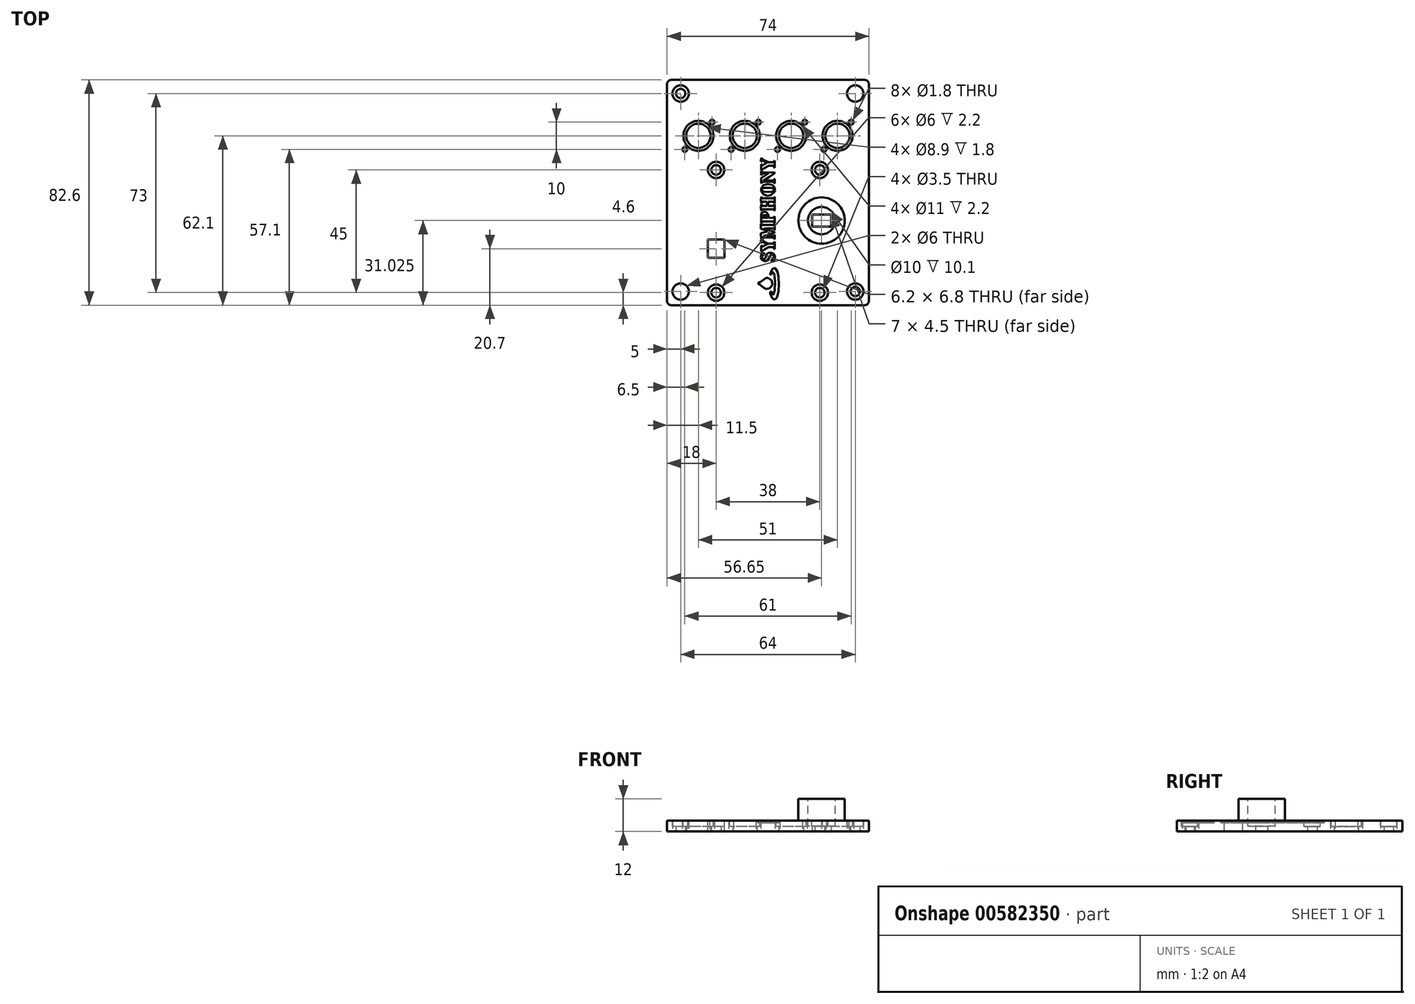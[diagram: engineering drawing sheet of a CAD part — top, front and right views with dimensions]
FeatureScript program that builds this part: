
annotation { "Feature Type Name" : "Feature", "Feature Type Description" : "" }
export const myFeature = defineFeature(function(context is Context, id is Id, definition is map)
    precondition{}
    {
        {
            var Q0;
            Q0=qCreatedBy(makeId("Top.planeOp"),FACE);
            var sketch = newSketch(context, id + "F0", { "sketchPlane" : qUnion([Q0])});
            skLineSegment(sketch, "E0.bottom", {"start": v(22.5, -9) * mm, "end": v(22.5, -61) * mm, "construction": true});
            skLineSegment(sketch, "E0.top", {"start": v(-22.5, -9) * mm, "end": v(-22.5, -61) * mm, "construction": true});
            skLineSegment(sketch, "E0.left", {"start": v(22.5, -9) * mm, "end": v(-22.5, -9) * mm, "construction": true});
            skLineSegment(sketch, "E0.right", {"start": v(22.5, -61) * mm, "end": v(-22.5, -61) * mm, "construction": true});
            skPoint(sketch, "E0.middle", {"position": v(0, -35) * mm});
            skCircle(sketch, "E1", {"center": v(-19, -57.5) * mm, "radius": 1.5 * mm, "construction": true});
            skCircle(sketch, "E2.cCircle", {"center": v(-19, -57.5) * mm, "radius": 2.75 * mm, "construction": true});
            skLineSegment(sketch, "E2.0", {"start": v(-20.59, -54.75) * mm, "end": v(-17.41, -54.75) * mm, "construction": true});
            skLineSegment(sketch, "E2.1", {"start": v(-17.41, -54.75) * mm, "end": v(-15.82, -57.5) * mm, "construction": true});
            skLineSegment(sketch, "E2.2", {"start": v(-15.82, -57.5) * mm, "end": v(-17.41, -60.25) * mm, "construction": true});
            skLineSegment(sketch, "E2.3", {"start": v(-17.41, -60.25) * mm, "end": v(-20.59, -60.25) * mm, "construction": true});
            skLineSegment(sketch, "E2.4", {"start": v(-20.59, -60.25) * mm, "end": v(-22.18, -57.5) * mm, "construction": true});
            skLineSegment(sketch, "E2.5", {"start": v(-22.18, -57.5) * mm, "end": v(-20.59, -54.75) * mm, "construction": true});
            skPoint(sketch, "E2.0.midPoint", {"position": v(-19, -54.75) * mm});
            skLineSegment(sketch, "E3.MirrorCS", {"start": v(-20.59, -15.25) * mm, "end": v(-17.41, -15.25) * mm, "construction": true});
            skCircle(sketch, "E4.MirrorC", {"center": v(-19, -12.5) * mm, "radius": 1.5 * mm, "construction": true});
            skCircle(sketch, "E5.MirrorC", {"center": v(-19, -12.5) * mm, "radius": 2.75 * mm, "construction": true});
            skLineSegment(sketch, "E6.MirrorCS", {"start": v(-17.41, -15.25) * mm, "end": v(-15.82, -12.5) * mm, "construction": true});
            skPoint(sketch, "E7.MirrorP", {"position": v(-19, -15.25) * mm});
            skLineSegment(sketch, "E8.MirrorCS", {"start": v(-22.18, -12.5) * mm, "end": v(-20.59, -15.25) * mm, "construction": true});
            skLineSegment(sketch, "E9.MirrorCS", {"start": v(-20.59, -9.75) * mm, "end": v(-22.18, -12.5) * mm, "construction": true});
            skLineSegment(sketch, "E10.MirrorCS", {"start": v(-15.82, -12.5) * mm, "end": v(-17.41, -9.75) * mm, "construction": true});
            skLineSegment(sketch, "E11.MirrorCS", {"start": v(-17.41, -9.75) * mm, "end": v(-20.59, -9.75) * mm, "construction": true});
            skLineSegment(sketch, "E12.MirrorCS", {"start": v(20.59, -15.25) * mm, "end": v(17.41, -15.25) * mm, "construction": true});
            skLineSegment(sketch, "E13.MirrorCS", {"start": v(22.18, -57.5) * mm, "end": v(20.59, -54.75) * mm, "construction": true});
            skLineSegment(sketch, "E14.MirrorCS", {"start": v(20.59, -60.25) * mm, "end": v(22.18, -57.5) * mm, "construction": true});
            skLineSegment(sketch, "E15.MirrorCS", {"start": v(15.82, -57.5) * mm, "end": v(17.41, -60.25) * mm, "construction": true});
            skLineSegment(sketch, "E16.MirrorCS", {"start": v(17.41, -54.75) * mm, "end": v(15.82, -57.5) * mm, "construction": true});
            skLineSegment(sketch, "E17.MirrorCS", {"start": v(20.59, -54.75) * mm, "end": v(17.41, -54.75) * mm, "construction": true});
            skLineSegment(sketch, "E18.MirrorCS", {"start": v(20.59, -9.75) * mm, "end": v(22.18, -12.5) * mm, "construction": true});
            skLineSegment(sketch, "E19.MirrorCS", {"start": v(17.41, -9.75) * mm, "end": v(20.59, -9.75) * mm, "construction": true});
            skLineSegment(sketch, "E20.MirrorCS", {"start": v(22.18, -12.5) * mm, "end": v(20.59, -15.25) * mm, "construction": true});
            skLineSegment(sketch, "E21.MirrorCS", {"start": v(15.82, -12.5) * mm, "end": v(17.41, -9.75) * mm, "construction": true});
            skLineSegment(sketch, "E22.MirrorCS", {"start": v(17.41, -15.25) * mm, "end": v(15.82, -12.5) * mm, "construction": true});
            skLineSegment(sketch, "E23.MirrorCS", {"start": v(17.41, -60.25) * mm, "end": v(20.59, -60.25) * mm, "construction": true});
            skCircle(sketch, "E24.MirrorC", {"center": v(19, -57.5) * mm, "radius": 2.75 * mm, "construction": true});
            skPoint(sketch, "E25.MirrorP", {"position": v(19, -15.25) * mm});
            skCircle(sketch, "E26.MirrorC", {"center": v(19, -57.5) * mm, "radius": 1.5 * mm, "construction": true});
            skCircle(sketch, "E27.MirrorC", {"center": v(19, -12.5) * mm, "radius": 2.75 * mm, "construction": true});
            skCircle(sketch, "E28.MirrorC", {"center": v(19, -12.5) * mm, "radius": 1.5 * mm, "construction": true});
            skPoint(sketch, "E29.MirrorP", {"position": v(19, -54.75) * mm});
            skLineSegment(sketch, "E30.bottom", {"start": v(16.9, -32.65) * mm, "end": v(16.9, -29.5) * mm, "construction": true});
            skLineSegment(sketch, "E30.top", {"start": v(22.4, -32.65) * mm, "end": v(22.4, -29.5) * mm, "construction": true});
            skLineSegment(sketch, "E30.left", {"start": v(16.9, -32.65) * mm, "end": v(22.4, -32.65) * mm, "construction": true});
            skLineSegment(sketch, "E30.right", {"start": v(16.9, -29.5) * mm, "end": v(22.4, -29.5) * mm, "construction": true});
            skLineSegment(sketch, "E31", {"start": v(16.9, -32.65) * mm, "end": v(22.4, -29.5) * mm, "construction": true});
            skLineSegment(sketch, "E32", {"start": v(16.9, -29.5) * mm, "end": v(22.4, -32.65) * mm, "construction": true});
            skSolve(sketch);
        }
        {
            var Q0;
            Q0=qCreatedBy(makeId("Top.planeOp"),FACE);
            var sketch = newSketch(context, id + "F1", { "sketchPlane" : qUnion([Q0])});
            skLineSegment(sketch, "E33.bottom", {"start": v(-18, -7.5) * mm, "end": v(-33, -7.5) * mm, "construction": true});
            skLineSegment(sketch, "E33.top", {"start": v(-18, 7.5) * mm, "end": v(-33, 7.5) * mm, "construction": true});
            skLineSegment(sketch, "E33.left", {"start": v(-18, -7.5) * mm, "end": v(-18, 7.5) * mm, "construction": true});
            skLineSegment(sketch, "E33.right", {"start": v(-33, -7.5) * mm, "end": v(-33, 7.5) * mm, "construction": true});
            skCircle(sketch, "E34", {"center": v(-30.5, 5) * mm, "radius": 0.9 * mm});
            skCircle(sketch, "E35.MirrorC", {"center": v(-20.5, 5) * mm, "radius": 0.9 * mm});
            skCircle(sketch, "E36.MirrorC", {"center": v(-30.5, -5) * mm, "radius": 0.9 * mm});
            skCircle(sketch, "E37.MirrorC", {"center": v(-20.5, -5) * mm, "radius": 0.9 * mm});
            skCircle(sketch, "E38.1.0.0", {"center": v(-13.5, -5) * mm, "radius": 0.9 * mm});
            skCircle(sketch, "E38.1.0.1", {"center": v(-13.5, 5) * mm, "radius": 0.9 * mm});
            skLineSegment(sketch, "E38.1.0.2", {"start": v(-16, -7.5) * mm, "end": v(-16, 7.5) * mm, "construction": true});
            skLineSegment(sketch, "E38.1.0.3", {"start": v(-1, -7.5) * mm, "end": v(-1, 7.5) * mm, "construction": true});
            skCircle(sketch, "E38.1.0.4", {"center": v(-3.5, 5) * mm, "radius": 0.9 * mm});
            skCircle(sketch, "E38.1.0.5", {"center": v(-3.5, -5) * mm, "radius": 0.9 * mm});
            skLineSegment(sketch, "E38.1.0.6", {"start": v(-1, -7.5) * mm, "end": v(-16, -7.5) * mm, "construction": true});
            skLineSegment(sketch, "E38.1.0.7", {"start": v(-1, 7.5) * mm, "end": v(-16, 7.5) * mm, "construction": true});
            skCircle(sketch, "E38.2.0.0", {"center": v(3.5, -5) * mm, "radius": 0.9 * mm});
            skCircle(sketch, "E38.2.0.1", {"center": v(3.5, 5) * mm, "radius": 0.9 * mm});
            skLineSegment(sketch, "E38.2.0.2", {"start": v(1, -7.5) * mm, "end": v(1, 7.5) * mm, "construction": true});
            skLineSegment(sketch, "E38.2.0.3", {"start": v(16, -7.5) * mm, "end": v(16, 7.5) * mm, "construction": true});
            skCircle(sketch, "E38.2.0.4", {"center": v(13.5, 5) * mm, "radius": 0.9 * mm});
            skCircle(sketch, "E38.2.0.5", {"center": v(13.5, -5) * mm, "radius": 0.9 * mm});
            skLineSegment(sketch, "E38.2.0.6", {"start": v(16, -7.5) * mm, "end": v(1, -7.5) * mm, "construction": true});
            skLineSegment(sketch, "E38.2.0.7", {"start": v(16, 7.5) * mm, "end": v(1, 7.5) * mm, "construction": true});
            skCircle(sketch, "E38.3.0.0", {"center": v(20.5, -5) * mm, "radius": 0.9 * mm});
            skCircle(sketch, "E38.3.0.1", {"center": v(20.5, 5) * mm, "radius": 0.9 * mm});
            skLineSegment(sketch, "E38.3.0.2", {"start": v(18, -7.5) * mm, "end": v(18, 7.5) * mm, "construction": true});
            skLineSegment(sketch, "E38.3.0.3", {"start": v(33, -7.5) * mm, "end": v(33, 7.5) * mm, "construction": true});
            skCircle(sketch, "E38.3.0.4", {"center": v(30.5, 5) * mm, "radius": 0.9 * mm});
            skCircle(sketch, "E38.3.0.5", {"center": v(30.5, -5) * mm, "radius": 0.9 * mm});
            skLineSegment(sketch, "E38.3.0.6", {"start": v(33, -7.5) * mm, "end": v(18, -7.5) * mm, "construction": true});
            skLineSegment(sketch, "E38.3.0.7", {"start": v(33, 7.5) * mm, "end": v(18, 7.5) * mm, "construction": true});
            skLineSegment(sketch, "E38.direction1", {"start": v(-33, -7.5) * mm, "end": v(-16, -7.5) * mm, "construction": true});
            skLineSegment(sketch, "E39.top", {"start": v(-37, -62.1) * mm, "end": v(37, -62.1) * mm});
            skLineSegment(sketch, "E39.left", {"start": v(-37, 10.5) * mm, "end": v(-37, -62.1) * mm});
            skLineSegment(sketch, "E39.right", {"start": v(37, 10.5) * mm, "end": v(37, -62.1) * mm});
            skPoint(sketch, "E40.0", {"position": v(-19, -12.5) * mm});
            skCircle(sketch, "E41", {"center": v(-19, -12.5) * mm, "radius": 1.75 * mm});
            skCircle(sketch, "E42.MirrorC", {"center": v(19, -12.5) * mm, "radius": 1.75 * mm});
            skCircle(sketch, "E43.MirrorC", {"center": v(19, -57.5) * mm, "radius": 1.75 * mm});
            skCircle(sketch, "E44.MirrorC", {"center": v(-19, -57.5) * mm, "radius": 1.75 * mm});
            skLineSegment(sketch, "E45.direction1", {"start": v(-25.5, 0) * mm, "end": v(-8.5, 0) * mm, "construction": true});
            skLineSegment(sketch, "E46.top", {"start": v(-37, 20.5) * mm, "end": v(37, 20.5) * mm});
            skLineSegment(sketch, "E46.left", {"start": v(-37, 10.5) * mm, "end": v(-37, 20.5) * mm});
            skLineSegment(sketch, "E46.right", {"start": v(37, 10.5) * mm, "end": v(37, 20.5) * mm});
            skCircle(sketch, "E47", {"center": v(-32, 15.5) * mm, "radius": 1.7 * mm});
            skCircle(sketch, "E48", {"center": v(-32, 15.5) * mm, "radius": 3 * mm});
            skCircle(sketch, "E49.MirrorC", {"center": v(32, 15.5) * mm, "radius": 3 * mm});
            skCircle(sketch, "E50.MirrorC", {"center": v(32, 15.5) * mm, "radius": 1.7 * mm});
            skLineSegment(sketch, "E51", {"start": v(-37, -20.8) * mm, "end": v(37, -20.8) * mm, "construction": true});
            skCircle(sketch, "E52.MirrorC", {"center": v(32, -57.1) * mm, "radius": 1.7 * mm});
            skCircle(sketch, "E53.MirrorC", {"center": v(32, -57.1) * mm, "radius": 3 * mm});
            skCircle(sketch, "E54.MirrorC", {"center": v(-32, -57.1) * mm, "radius": 3 * mm});
            skCircle(sketch, "E55.MirrorC", {"center": v(-32, -57.1) * mm, "radius": 1.7 * mm});
            skCircle(sketch, "E56", {"center": v(-25.5, 0) * mm, "radius": 4.45 * mm});
            skCircle(sketch, "E57.1.0.0", {"center": v(-8.5, 0) * mm, "radius": 4.45 * mm});
            skCircle(sketch, "E57.2.0.0", {"center": v(8.5, 0) * mm, "radius": 4.45 * mm});
            skCircle(sketch, "E57.3.0.0", {"center": v(25.5, 0) * mm, "radius": 4.45 * mm});
            skPoint(sketch, "E58.0", {"position": v(19.65, -31.08) * mm});
            skLineSegment(sketch, "E59.bottom", {"start": v(23.15, -33.33) * mm, "end": v(16.15, -33.33) * mm});
            skLineSegment(sketch, "E59.top", {"start": v(23.15, -28.83) * mm, "end": v(16.15, -28.83) * mm});
            skLineSegment(sketch, "E59.left", {"start": v(23.15, -33.33) * mm, "end": v(23.15, -28.83) * mm});
            skLineSegment(sketch, "E59.right", {"start": v(16.15, -33.33) * mm, "end": v(16.15, -28.83) * mm});
            skCircle(sketch, "E60", {"center": v(19.65, -31.08) * mm, "radius": 5 * mm});
            skCircle(sketch, "E61", {"center": v(19.65, -31.08) * mm, "radius": 8.5 * mm});
            skSolve(sketch);
        }
        {
            var Q0;
            Q0=makeQuery(id+"F1.imprint","IMPRINT",FACE,{"disambiguationData":[TD([[makeQuery(id+"F1.imprint","IMPRINT",EDGE,{"derivedFrom":sQuery(id+"F1.wireOp",EDGE,"E34")}),-1.0]])]});
            var Q1;
            Q1=makeQuery(id+"F1.imprint","IMPRINT",FACE,{"disambiguationData":[TD([[makeQuery(id+"F1.imprint","IMPRINT",EDGE,{"derivedFrom":sQuery(id+"F1.wireOp",EDGE,"E47")}),-1.0]])]});
            var Q2;
            Q2=makeQuery(id+"F1.imprint","IMPRINT",FACE,{"disambiguationData":[TD([[makeQuery(id+"F1.imprint","IMPRINT",EDGE,{"derivedFrom":sQuery(id+"F1.wireOp",EDGE,"E49.MirrorC")}),-1.0]])]});
            var Q3;
            Q3=makeQuery(id+"F1.imprint","IMPRINT",FACE,{"disambiguationData":[TD([[makeQuery(id+"F1.imprint","IMPRINT",EDGE,{"derivedFrom":sQuery(id+"F1.wireOp",EDGE,"E54.MirrorC")}),-1.0]])]});
            var Q4;
            Q4=makeQuery(id+"F1.imprint","IMPRINT",FACE,{"disambiguationData":[TD([[makeQuery(id+"F1.imprint","IMPRINT",EDGE,{"derivedFrom":sQuery(id+"F1.wireOp",EDGE,"E52.MirrorC")}),-1.0]])]});
            var Q5;
            Q5=makeQuery(id+"F1.imprint","IMPRINT",FACE,{"disambiguationData":[TD([[makeQuery(id+"F1.imprint","IMPRINT",EDGE,{"derivedFrom":sQuery(id+"F1.wireOp",EDGE,"E34")}),1.0]])]});
            var Q6;
            Q6=makeQuery(id+"F1.imprint","IMPRINT",FACE,{"disambiguationData":[TD([[makeQuery(id+"F1.imprint","IMPRINT",EDGE,{"derivedFrom":sQuery(id+"F1.wireOp",EDGE,"E38.2.0.0")}),-1.0]])]});
            var Q7;
            Q7=makeQuery(id+"F1.imprint","IMPRINT",FACE,{"disambiguationData":[TD([[makeQuery(id+"F1.imprint","IMPRINT",EDGE,{"derivedFrom":sQuery(id+"F1.wireOp",EDGE,"E36.MirrorC")}),-1.0]])]});
            var Q8;
            Q8=makeQuery(id+"F1.imprint","IMPRINT",FACE,{"disambiguationData":[TD([[makeQuery(id+"F1.imprint","IMPRINT",EDGE,{"derivedFrom":sQuery(id+"F1.wireOp",EDGE,"E37.MirrorC")}),1.0]])]});
            var Q9;
            Q9=makeQuery(id+"F1.imprint","IMPRINT",FACE,{"disambiguationData":[TD([[makeQuery(id+"F1.imprint","IMPRINT",EDGE,{"derivedFrom":sQuery(id+"F1.wireOp",EDGE,"E38.1.0.0")}),-1.0]])]});
            var Q10;
            Q10=makeQuery(id+"F1.imprint","IMPRINT",FACE,{"disambiguationData":[TD([[makeQuery(id+"F1.imprint","IMPRINT",EDGE,{"derivedFrom":sQuery(id+"F1.wireOp",EDGE,"E38.1.0.5")}),1.0]])]});
            var Q11;
            Q11=makeQuery(id+"F1.imprint","IMPRINT",FACE,{"disambiguationData":[TD([[makeQuery(id+"F1.imprint","IMPRINT",EDGE,{"derivedFrom":sQuery(id+"F1.wireOp",EDGE,"E38.2.0.12")}),1.0]])]});
            var Q12;
            Q12=makeQuery(id+"F1.imprint","IMPRINT",FACE,{"disambiguationData":[TD([[makeQuery(id+"F1.imprint","IMPRINT",EDGE,{"derivedFrom":sQuery(id+"F1.wireOp",EDGE,"E38.1.0.12")}),1.0]])]});
            var Q13;
            Q13=makeQuery(id+"F1.imprint","IMPRINT",FACE,{"disambiguationData":[TD([[makeQuery(id+"F1.imprint","IMPRINT",EDGE,{"derivedFrom":sQuery(id+"F1.wireOp",EDGE,"0d3dec74-ecaa-4266-b990-dcd2288d9d95")}),1.0]])]});
            var Q14;
            Q14=makeQuery(id+"F1.imprint","IMPRINT",FACE,{"disambiguationData":[TD([[makeQuery(id+"F1.imprint","IMPRINT",EDGE,{"derivedFrom":sQuery(id+"F1.wireOp",EDGE,"f5867afd-0dbe-4015-8089-30a12c86c954")}),1.0]])]});
            var Q15;
            Q15=makeQuery(id+"F1.imprint","IMPRINT",FACE,{"disambiguationData":[TD([[makeQuery(id+"F1.imprint","IMPRINT",EDGE,{"derivedFrom":sQuery(id+"F1.wireOp",EDGE,"70b2c587-75d0-4c69-bc02-c068b628aa1f")}),1.0]])]});
            var Q16;
            Q16=makeQuery(id+"F1.imprint","IMPRINT",FACE,{"disambiguationData":[TD([[makeQuery(id+"F1.imprint","IMPRINT",EDGE,{"derivedFrom":sQuery(id+"F1.wireOp",EDGE,"E38.1.0.10")}),1.0]])]});
            var Q17;
            Q17=makeQuery(id+"F1.imprint","IMPRINT",FACE,{"disambiguationData":[TD([[makeQuery(id+"F1.imprint","IMPRINT",EDGE,{"derivedFrom":sQuery(id+"F1.wireOp",EDGE,"E38.1.0.11")}),1.0]])]});
            var Q18;
            Q18=makeQuery(id+"F1.imprint","IMPRINT",FACE,{"disambiguationData":[TD([[makeQuery(id+"F1.imprint","IMPRINT",EDGE,{"derivedFrom":sQuery(id+"F1.wireOp",EDGE,"E38.2.0.10")}),1.0]])]});
            var Q19;
            Q19=makeQuery(id+"F1.imprint","IMPRINT",FACE,{"disambiguationData":[TD([[makeQuery(id+"F1.imprint","IMPRINT",EDGE,{"derivedFrom":sQuery(id+"F1.wireOp",EDGE,"E38.2.0.11")}),1.0]])]});
            var Q20;
            Q20=makeQuery(id+"F1.imprint","IMPRINT",FACE,{"disambiguationData":[TD([[makeQuery(id+"F1.imprint","IMPRINT",EDGE,{"derivedFrom":sQuery(id+"F1.wireOp",EDGE,"E38.3.0.0")}),-1.0]])]});
            var Q21;
            Q21=makeQuery(id+"F1.imprint","IMPRINT",FACE,{"disambiguationData":[TD([[makeQuery(id+"F1.imprint","IMPRINT",EDGE,{"derivedFrom":sQuery(id+"F1.wireOp",EDGE,"E38.3.0.1")}),1.0]])]});
            var Q22;
            Q22=makeQuery(id+"F1.imprint","IMPRINT",FACE,{"disambiguationData":[TD([[makeQuery(id+"F1.imprint","IMPRINT",EDGE,{"derivedFrom":sQuery(id+"F1.wireOp",EDGE,"0d3dec74-ecaa-4266-b990-dcd2288d9d95")}),-1.0]])]});
            var Q23;
            Q23=makeQuery(id+"F1.imprint","IMPRINT",FACE,{"disambiguationData":[TD([[makeQuery(id+"F1.imprint","IMPRINT",EDGE,{"derivedFrom":sQuery(id+"F1.wireOp",EDGE,"E38.1.0.10")}),-1.0]])]});
            var Q24;
            Q24=makeQuery(id+"F1.imprint","IMPRINT",FACE,{"disambiguationData":[TD([[makeQuery(id+"F1.imprint","IMPRINT",EDGE,{"derivedFrom":sQuery(id+"F1.wireOp",EDGE,"E38.2.0.10")}),-1.0]])]});
            var Q25;
            Q25=makeQuery(id+"F1.imprint","IMPRINT",FACE,{"disambiguationData":[TD([[makeQuery(id+"F1.imprint","IMPRINT",EDGE,{"derivedFrom":sQuery(id+"F1.wireOp",EDGE,"E38.2.0.4")}),-1.0]])]});
            var Q26;
            Q26=makeQuery(id+"F1.imprint","IMPRINT",FACE,{"disambiguationData":[TD([[makeQuery(id+"F1.imprint","IMPRINT",EDGE,{"derivedFrom":sQuery(id+"F1.wireOp",EDGE,"E38.2.0.1")}),1.0]])]});
            var Q27;
            Q27=makeQuery(id+"F1.imprint","IMPRINT",FACE,{"disambiguationData":[TD([[makeQuery(id+"F1.imprint","IMPRINT",EDGE,{"derivedFrom":sQuery(id+"F1.wireOp",EDGE,"E35.MirrorC")}),-1.0]])]});
            var Q28;
            Q28=makeQuery(id+"F1.imprint","IMPRINT",FACE,{"disambiguationData":[TD([[makeQuery(id+"F1.imprint","IMPRINT",EDGE,{"derivedFrom":sQuery(id+"F1.wireOp",EDGE,"E38.2.0.5")}),1.0]])]});
            var Q29;
            Q29=makeQuery(id+"F1.imprint","IMPRINT",FACE,{"disambiguationData":[TD([[makeQuery(id+"F1.imprint","IMPRINT",EDGE,{"derivedFrom":sQuery(id+"F1.wireOp",EDGE,"E38.1.0.1")}),1.0]])]});
            var Q30;
            Q30=makeQuery(id+"F1.imprint","IMPRINT",FACE,{"disambiguationData":[TD([[makeQuery(id+"F1.imprint","IMPRINT",EDGE,{"derivedFrom":sQuery(id+"F1.wireOp",EDGE,"E38.1.0.4")}),-1.0]])]});
            var Q31;
            Q31=makeQuery(id+"F1.imprint","IMPRINT",FACE,{"disambiguationData":[TD([[makeQuery(id+"F1.imprint","IMPRINT",EDGE,{"derivedFrom":sQuery(id+"F1.wireOp",EDGE,"E38.3.0.4")}),-1.0]])]});
            var Q32;
            Q32=makeQuery(id+"F1.imprint","IMPRINT",FACE,{"disambiguationData":[TD([[makeQuery(id+"F1.imprint","IMPRINT",EDGE,{"derivedFrom":sQuery(id+"F1.wireOp",EDGE,"E38.3.0.5")}),1.0]])]});
            var Q33;
            Q33=makeQuery(id+"F1.imprint","IMPRINT",FACE,{"disambiguationData":[TD([[makeQuery(id+"F1.imprint","IMPRINT",EDGE,{"derivedFrom":sQuery(id+"F1.wireOp",EDGE,"E38.3.0.10")}),-1.0]])]});
            var Q34;
            Q34=makeQuery(id+"F1.imprint","IMPRINT",FACE,{"disambiguationData":[TD([[makeQuery(id+"F1.imprint","IMPRINT",EDGE,{"derivedFrom":sQuery(id+"F1.wireOp",EDGE,"E38.3.0.10")}),1.0]])]});
            var Q35;
            Q35=makeQuery(id+"F1.imprint","IMPRINT",FACE,{"disambiguationData":[TD([[makeQuery(id+"F1.imprint","IMPRINT",EDGE,{"derivedFrom":sQuery(id+"F1.wireOp",EDGE,"E38.3.0.11")}),1.0]])]});
            var Q36;
            Q36=makeQuery(id+"F1.imprint","IMPRINT",FACE,{"disambiguationData":[TD([[makeQuery(id+"F1.imprint","IMPRINT",EDGE,{"derivedFrom":sQuery(id+"F1.wireOp",EDGE,"E38.3.0.12")}),1.0]])]});
            var Q37;
            Q37=makeQuery(id+"F1.imprint","IMPRINT",FACE,{"disambiguationData":[TD([[makeQuery(id+"F1.imprint","IMPRINT",EDGE,{"derivedFrom":sQuery(id+"F1.wireOp",EDGE,"E60")}),-1.0]])]});
            var Q38;
            Q38=makeQuery(id+"F1.imprint","IMPRINT",FACE,{"disambiguationData":[TD([[makeQuery(id+"F1.imprint","IMPRINT",EDGE,{"derivedFrom":sQuery(id+"F1.wireOp",EDGE,"E59.bottom")}),1.0]])]});
            extrude(context, id + "F2", {"entities" : qUnion([Q0, Q1, Q2, Q3, Q4, Q5, Q6, Q7, Q8, Q9, Q10, Q11, Q12, Q13, Q14, Q15, Q16, Q17, Q18, Q19, Q20, Q21, Q22, Q23, Q24, Q25, Q26, Q27, Q28, Q29, Q30, Q31, Q32, Q33, Q34, Q35, Q36, Q37, Q38]), "depth" : 4 * mm, "offsetDistance" : 25 * mm});
        }
        {
            var Q0;
            Q0=makeQuery(id+"F2.opExtrude","SWEPT_EDGE",EDGE,{"disambiguationData":[OSD([sQuery(id+"F1.wireOp",EDGE,"E39.top"),sQuery(id+"F1.wireOp",EDGE,"E39.left")])]});
            var Q1;
            Q1=makeQuery(id+"F2.opExtrude","SWEPT_EDGE",EDGE,{"disambiguationData":[OSD([sQuery(id+"F1.wireOp",EDGE,"E39.top"),sQuery(id+"F1.wireOp",EDGE,"E39.right")])]});
            var Q2;
            Q2=makeQuery(id+"F2.opExtrude","SWEPT_EDGE",EDGE,{"disambiguationData":[OSD([sQuery(id+"F1.wireOp",EDGE,"E46.top"),sQuery(id+"F1.wireOp",EDGE,"E46.right")])]});
            var Q3;
            Q3=makeQuery(id+"F2.opExtrude","SWEPT_EDGE",EDGE,{"disambiguationData":[OSD([sQuery(id+"F1.wireOp",EDGE,"E46.top"),sQuery(id+"F1.wireOp",EDGE,"E46.left")])]});
            fillet(context, id + "F3", {"entities" : qUnion([Q0, Q1, Q2, Q3]), "radius" : 1.5 * mm, "tangentPropagation" : true, "allowEdgeOverflow" : false});
        }
        {
            var Q0;
            Q0=makeQuery(id+"F2.opExtrude","CAP_FACE",FACE,{"disambiguationData":[OSD([sQuery(id+"F1.wireOp",EDGE,"E39.top"),sQuery(id+"F1.wireOp",EDGE,"E39.left"),sQuery(id+"F1.wireOp",EDGE,"E39.right"),sQuery(id+"F1.wireOp",EDGE,"ZtF59OV2-kfJq-xDQm-ky9b-vxAiDFjwtKrt.bottom"),sQuery(id+"F1.wireOp",EDGE,"ZtF59OV2-kfJq-xDQm-ky9b-vxAiDFjwtKrt.top"),sQuery(id+"F1.wireOp",EDGE,"ZtF59OV2-kfJq-xDQm-ky9b-vxAiDFjwtKrt.left"),sQuery(id+"F1.wireOp",EDGE,"ZtF59OV2-kfJq-xDQm-ky9b-vxAiDFjwtKrt.right"),sQuery(id+"F1.wireOp",EDGE,"OfxVgRd8-8Rll-FesW-K7WL-WmYAdUh40JBy.bottom"),sQuery(id+"F1.wireOp",EDGE,"OfxVgRd8-8Rll-FesW-K7WL-WmYAdUh40JBy.top"),sQuery(id+"F1.wireOp",EDGE,"OfxVgRd8-8Rll-FesW-K7WL-WmYAdUh40JBy.left"),sQuery(id+"F1.wireOp",EDGE,"OfxVgRd8-8Rll-FesW-K7WL-WmYAdUh40JBy.right"),sQuery(id+"F1.wireOp",EDGE,"5421b44d-8772-4a96-8ed2-b48facbd643a.trimOffspring"),sQuery(id+"F1.wireOp",EDGE,"446a1e51-2a2d-4a3d-b0c0-7d5b57a94e87.trimOffspring"),sQuery(id+"F1.wireOp",EDGE,"e6be4eb3-bc97-4f03-aafd-c3c38b5d689d.trimOffspring"),sQuery(id+"F1.wireOp",EDGE,"9b8aff40-883d-4fe7-9ef0-59bda9a35524.trimOffspring"),sQuery(id+"F1.wireOp",EDGE,"E41"),sQuery(id+"F1.wireOp",EDGE,"E42.MirrorC"),sQuery(id+"F1.wireOp",EDGE,"E43.MirrorC"),sQuery(id+"F1.wireOp",EDGE,"E44.MirrorC"),sQuery(id+"F1.wireOp",EDGE,"E46.top"),sQuery(id+"F1.wireOp",EDGE,"E46.left"),sQuery(id+"F1.wireOp",EDGE,"E46.right"),sQuery(id+"F1.wireOp",EDGE,"E47"),sQuery(id+"F1.wireOp",EDGE,"E50.MirrorC"),sQuery(id+"F1.wireOp",EDGE,"E52.MirrorC"),sQuery(id+"F1.wireOp",EDGE,"E55.MirrorC"),sQuery(id+"F1.wireOp",EDGE,"E56"),sQuery(id+"F1.wireOp",EDGE,"E57.1.0.0"),sQuery(id+"F1.wireOp",EDGE,"E57.2.0.0"),sQuery(id+"F1.wireOp",EDGE,"E57.3.0.0")])],"isStart":false});
            var sketch = newSketch(context, id + "F4", { "sketchPlane" : qUnion([Q0])});
            skCircle(sketch, "E62.0", {"center": v(-32, -57.1) * mm, "radius": 3 * mm});
            skCircle(sketch, "E63.0", {"center": v(-32, 15.5) * mm, "radius": 3 * mm});
            skCircle(sketch, "E64.0", {"center": v(32, 15.5) * mm, "radius": 3 * mm});
            skCircle(sketch, "E65.0", {"center": v(32, -57.1) * mm, "radius": 3 * mm});
            skCircle(sketch, "E66.0", {"center": v(-19, -57.5) * mm, "radius": 3 * mm});
            skCircle(sketch, "E67.0", {"center": v(19, -57.5) * mm, "radius": 3 * mm});
            skCircle(sketch, "E68.0", {"center": v(19, -12.5) * mm, "radius": 3 * mm});
            skCircle(sketch, "E69.0", {"center": v(-19, -12.5) * mm, "radius": 3 * mm});
            skSolve(sketch);
        }
        {
            var Q0;
            Q0 = qSketchRegion(id + "F4", true);
            extrude(context, id + "F5", {"entities" : qUnion([Q0]), "operationType" : NewBodyOperationType.REMOVE, "oppositeDirection" : true, "depth" : 2.2 * mm, "offsetDistance" : 25 * mm});
        }
        {
            var Q0;
            Q0=makeQuery(id+"F2.opExtrude","CAP_FACE",FACE,{"disambiguationData":[OSD([sQuery(id+"F1.wireOp",EDGE,"E39.top"),sQuery(id+"F1.wireOp",EDGE,"E39.left"),sQuery(id+"F1.wireOp",EDGE,"E39.right"),sQuery(id+"F1.wireOp",EDGE,"ZtF59OV2-kfJq-xDQm-ky9b-vxAiDFjwtKrt.bottom"),sQuery(id+"F1.wireOp",EDGE,"ZtF59OV2-kfJq-xDQm-ky9b-vxAiDFjwtKrt.top"),sQuery(id+"F1.wireOp",EDGE,"ZtF59OV2-kfJq-xDQm-ky9b-vxAiDFjwtKrt.left"),sQuery(id+"F1.wireOp",EDGE,"ZtF59OV2-kfJq-xDQm-ky9b-vxAiDFjwtKrt.right"),sQuery(id+"F1.wireOp",EDGE,"OfxVgRd8-8Rll-FesW-K7WL-WmYAdUh40JBy.bottom"),sQuery(id+"F1.wireOp",EDGE,"OfxVgRd8-8Rll-FesW-K7WL-WmYAdUh40JBy.top"),sQuery(id+"F1.wireOp",EDGE,"OfxVgRd8-8Rll-FesW-K7WL-WmYAdUh40JBy.left"),sQuery(id+"F1.wireOp",EDGE,"OfxVgRd8-8Rll-FesW-K7WL-WmYAdUh40JBy.right"),sQuery(id+"F1.wireOp",EDGE,"5421b44d-8772-4a96-8ed2-b48facbd643a.trimOffspring"),sQuery(id+"F1.wireOp",EDGE,"446a1e51-2a2d-4a3d-b0c0-7d5b57a94e87.trimOffspring"),sQuery(id+"F1.wireOp",EDGE,"e6be4eb3-bc97-4f03-aafd-c3c38b5d689d.trimOffspring"),sQuery(id+"F1.wireOp",EDGE,"9b8aff40-883d-4fe7-9ef0-59bda9a35524.trimOffspring"),sQuery(id+"F1.wireOp",EDGE,"E41"),sQuery(id+"F1.wireOp",EDGE,"E42.MirrorC"),sQuery(id+"F1.wireOp",EDGE,"E43.MirrorC"),sQuery(id+"F1.wireOp",EDGE,"E44.MirrorC"),sQuery(id+"F1.wireOp",EDGE,"E46.top"),sQuery(id+"F1.wireOp",EDGE,"E46.left"),sQuery(id+"F1.wireOp",EDGE,"E46.right"),sQuery(id+"F1.wireOp",EDGE,"E47"),sQuery(id+"F1.wireOp",EDGE,"E50.MirrorC"),sQuery(id+"F1.wireOp",EDGE,"E52.MirrorC"),sQuery(id+"F1.wireOp",EDGE,"E55.MirrorC"),sQuery(id+"F1.wireOp",EDGE,"E56"),sQuery(id+"F1.wireOp",EDGE,"E57.1.0.0"),sQuery(id+"F1.wireOp",EDGE,"E57.2.0.0"),sQuery(id+"F1.wireOp",EDGE,"E57.3.0.0")])],"isStart":false});
            var sketch = newSketch(context, id + "F6", { "sketchPlane" : qUnion([Q0])});
            skPoint(sketch, "E70.0", {"position": v(-25.5, 0) * mm});
            skCircle(sketch, "E71", {"center": v(-25.5, 0) * mm, "radius": 5.5 * mm});
            skCircle(sketch, "E72.1.0.0", {"center": v(-8.5, 0) * mm, "radius": 5.5 * mm});
            skCircle(sketch, "E72.2.0.0", {"center": v(8.5, 0) * mm, "radius": 5.5 * mm});
            skCircle(sketch, "E72.3.0.0", {"center": v(25.5, 0) * mm, "radius": 5.5 * mm});
            skLineSegment(sketch, "E72.direction1", {"start": v(-25.5, 0) * mm, "end": v(-8.5, 0) * mm, "construction": true});
            skSolve(sketch);
        }
        {
            var Q0;
            Q0=makeQuery(id+"F6.imprint","IMPRINT",FACE,{"disambiguationData":[TD([[makeQuery(id+"F6.imprint","IMPRINT",EDGE,{"derivedFrom":sQuery(id+"F6.wireOp",EDGE,"E71")}),1.0]])]});
            var Q1;
            Q1=makeQuery(id+"F6.imprint","IMPRINT",FACE,{"disambiguationData":[TD([[makeQuery(id+"F6.imprint","IMPRINT",EDGE,{"derivedFrom":sQuery(id+"F6.wireOp",EDGE,"E72.1.0.0")}),1.0]])]});
            var Q2;
            Q2=makeQuery(id+"F6.imprint","IMPRINT",FACE,{"disambiguationData":[TD([[makeQuery(id+"F6.imprint","IMPRINT",EDGE,{"derivedFrom":sQuery(id+"F6.wireOp",EDGE,"E72.2.0.0")}),1.0]])]});
            var Q3;
            Q3=makeQuery(id+"F6.imprint","IMPRINT",FACE,{"disambiguationData":[TD([[makeQuery(id+"F6.imprint","IMPRINT",EDGE,{"derivedFrom":sQuery(id+"F6.wireOp",EDGE,"E72.3.0.0")}),1.0]])]});
            extrude(context, id + "F7", {"entities" : qUnion([Q0, Q1, Q2, Q3]), "operationType" : NewBodyOperationType.REMOVE, "oppositeDirection" : true, "depth" : 2.2 * mm, "offsetDistance" : 25 * mm});
        }
        {
            var Q0;
            Q0=makeQuery(id+"F2.opExtrude","CAP_FACE",FACE,{"disambiguationData":[OSD([sQuery(id+"F1.wireOp",EDGE,"E39.top"),sQuery(id+"F1.wireOp",EDGE,"E39.left"),sQuery(id+"F1.wireOp",EDGE,"E39.right"),sQuery(id+"F1.wireOp",EDGE,"E41"),sQuery(id+"F1.wireOp",EDGE,"E42.MirrorC"),sQuery(id+"F1.wireOp",EDGE,"E43.MirrorC"),sQuery(id+"F1.wireOp",EDGE,"E44.MirrorC"),sQuery(id+"F1.wireOp",EDGE,"E46.top"),sQuery(id+"F1.wireOp",EDGE,"E46.left"),sQuery(id+"F1.wireOp",EDGE,"E46.right"),sQuery(id+"F1.wireOp",EDGE,"E47"),sQuery(id+"F1.wireOp",EDGE,"E50.MirrorC"),sQuery(id+"F1.wireOp",EDGE,"E52.MirrorC"),sQuery(id+"F1.wireOp",EDGE,"E55.MirrorC"),sQuery(id+"F1.wireOp",EDGE,"E56"),sQuery(id+"F1.wireOp",EDGE,"E57.1.0.0"),sQuery(id+"F1.wireOp",EDGE,"E57.2.0.0"),sQuery(id+"F1.wireOp",EDGE,"E57.3.0.0"),sQuery(id+"F1.wireOp",EDGE,"E59.bottom"),sQuery(id+"F1.wireOp",EDGE,"E59.top"),sQuery(id+"F1.wireOp",EDGE,"E59.left"),sQuery(id+"F1.wireOp",EDGE,"E59.right")])],"isStart":false});
            var sketch = newSketch(context, id + "F8", { "sketchPlane" : qUnion([Q0])});
            skLineSegment(sketch, "E73", {"start": v(-22.36, -2.87) * mm, "end": v(-22.36, -2.87) * mm});
            skLineSegment(sketch, "E74", {"start": v(-11.87, -2.43) * mm, "end": v(-11.87, -2.43) * mm});
            skLineSegment(sketch, "E75", {"start": v(18.96, -0.41) * mm, "end": v(18.96, -0.41) * mm});
            skLineSegment(sketch, "E76", {"start": v(-7.51, -2.34) * mm, "end": v(-7.51, -2.34) * mm});
            skLineSegment(sketch, "E77", {"start": v(-3.83, -2.27) * mm, "end": v(-3.83, -2.27) * mm});
            skLineSegment(sketch, "E78", {"start": v(2.06, -2.34) * mm, "end": v(2.06, -2.34) * mm});
            skLineSegment(sketch, "E79", {"start": v(22.32, -2.37) * mm, "end": v(22.32, -2.37) * mm});
            skLineSegment(sketch, "E80", {"start": v(3.85, -57.05) * mm, "end": v(3.3, -59.04) * mm});
            skLineSegment(sketch, "E81", {"start": v(3.3, -59.04) * mm, "end": v(2.8, -59.8) * mm});
            skLineSegment(sketch, "E82", {"start": v(2.8, -59.8) * mm, "end": v(2.1, -59.95) * mm});
            skLineSegment(sketch, "E83", {"start": v(2.1, -59.95) * mm, "end": v(1.42, -59.32) * mm});
            skLineSegment(sketch, "E84", {"start": v(1.42, -59.32) * mm, "end": v(0.85, -57.66) * mm});
            skLineSegment(sketch, "E85", {"start": v(0.85, -57.66) * mm, "end": v(0.82, -57.34) * mm});
            skLineSegment(sketch, "E86", {"start": v(0.82, -57.34) * mm, "end": v(0.94, -57.53) * mm});
            skLineSegment(sketch, "E87", {"start": v(0.94, -57.53) * mm, "end": v(1.28, -58.54) * mm});
            skLineSegment(sketch, "E88", {"start": v(1.28, -58.54) * mm, "end": v(1.74, -59.32) * mm});
            skLineSegment(sketch, "E89", {"start": v(1.74, -59.32) * mm, "end": v(2.16, -59.46) * mm});
            skLineSegment(sketch, "E90", {"start": v(2.16, -59.46) * mm, "end": v(2.6, -59.1) * mm});
            skLineSegment(sketch, "E91", {"start": v(2.6, -59.1) * mm, "end": v(3.07, -57.94) * mm});
            skLineSegment(sketch, "E92", {"start": v(3.07, -57.94) * mm, "end": v(3.46, -55.06) * mm});
            skLineSegment(sketch, "E93", {"start": v(3.46, -55.06) * mm, "end": v(3.4, -52.37) * mm});
            skLineSegment(sketch, "E94", {"start": v(3.4, -52.37) * mm, "end": v(2.88, -49.83) * mm});
            skLineSegment(sketch, "E95", {"start": v(2.88, -49.83) * mm, "end": v(2.4, -49.06) * mm});
            skLineSegment(sketch, "E96", {"start": v(2.4, -49.06) * mm, "end": v(1.92, -48.94) * mm});
            skLineSegment(sketch, "E97", {"start": v(1.92, -48.94) * mm, "end": v(1.44, -49.46) * mm});
            skLineSegment(sketch, "E98", {"start": v(1.44, -49.46) * mm, "end": v(1.07, -50.46) * mm});
            skLineSegment(sketch, "E99", {"start": v(1.07, -50.46) * mm, "end": v(0.86, -50.95) * mm});
            skLineSegment(sketch, "E100", {"start": v(0.86, -50.95) * mm, "end": v(0.81, -50.8) * mm});
            skLineSegment(sketch, "E101", {"start": v(0.81, -50.8) * mm, "end": v(1.14, -49.72) * mm});
            skLineSegment(sketch, "E102", {"start": v(1.14, -49.72) * mm, "end": v(1.54, -48.88) * mm});
            skLineSegment(sketch, "E103", {"start": v(1.54, -48.88) * mm, "end": v(2.21, -48.42) * mm});
            skLineSegment(sketch, "E104", {"start": v(2.21, -48.42) * mm, "end": v(2.9, -48.74) * mm});
            skLineSegment(sketch, "E105", {"start": v(2.9, -48.74) * mm, "end": v(3.46, -49.79) * mm});
            skLineSegment(sketch, "E106", {"start": v(3.46, -49.79) * mm, "end": v(3.86, -51.7) * mm});
            skLineSegment(sketch, "E107", {"start": v(3.86, -51.7) * mm, "end": v(3.95, -54.6) * mm});
            skLineSegment(sketch, "E108", {"start": v(3.95, -54.6) * mm, "end": v(3.9, -56.73) * mm});
            skLineSegment(sketch, "E109", {"start": v(3.9, -56.73) * mm, "end": v(3.85, -57.05) * mm});
            skLineSegment(sketch, "E110", {"start": v(2.97, -56.38) * mm, "end": v(2.58, -58.08) * mm});
            skLineSegment(sketch, "E111", {"start": v(2.58, -58.08) * mm, "end": v(2.18, -58.67) * mm});
            skLineSegment(sketch, "E112", {"start": v(2.18, -58.67) * mm, "end": v(1.91, -58.75) * mm});
            skLineSegment(sketch, "E113", {"start": v(1.91, -58.75) * mm, "end": v(1.44, -58.27) * mm});
            skLineSegment(sketch, "E114", {"start": v(1.44, -58.27) * mm, "end": v(1.09, -57.02) * mm});
            skLineSegment(sketch, "E115", {"start": v(1.09, -57.02) * mm, "end": v(1.16, -57.02) * mm});
            skLineSegment(sketch, "E116", {"start": v(1.16, -57.02) * mm, "end": v(1.48, -57.92) * mm});
            skLineSegment(sketch, "E117", {"start": v(1.48, -57.92) * mm, "end": v(1.78, -58.33) * mm});
            skLineSegment(sketch, "E118", {"start": v(1.78, -58.33) * mm, "end": v(2, -58.2) * mm});
            skLineSegment(sketch, "E119", {"start": v(2, -58.2) * mm, "end": v(2.47, -56.63) * mm});
            skLineSegment(sketch, "E120", {"start": v(2.47, -56.63) * mm, "end": v(2.61, -53.35) * mm});
            skLineSegment(sketch, "E121", {"start": v(2.61, -53.35) * mm, "end": v(2.34, -50.88) * mm});
            skLineSegment(sketch, "E122", {"start": v(2.34, -50.88) * mm, "end": v(2.02, -50.03) * mm});
            skLineSegment(sketch, "E123", {"start": v(2.02, -50.03) * mm, "end": v(1.77, -49.9) * mm});
            skLineSegment(sketch, "E124", {"start": v(1.77, -49.9) * mm, "end": v(1.5, -50.25) * mm});
            skLineSegment(sketch, "E125", {"start": v(1.5, -50.25) * mm, "end": v(1.23, -50.84) * mm});
            skLineSegment(sketch, "E126", {"start": v(1.23, -50.84) * mm, "end": v(1.18, -50.7) * mm});
            skLineSegment(sketch, "E127", {"start": v(1.18, -50.7) * mm, "end": v(1.48, -49.9) * mm});
            skLineSegment(sketch, "E128", {"start": v(1.48, -49.9) * mm, "end": v(1.89, -49.55) * mm});
            skLineSegment(sketch, "E129", {"start": v(1.89, -49.55) * mm, "end": v(2.34, -49.71) * mm});
            skLineSegment(sketch, "E130", {"start": v(2.34, -49.71) * mm, "end": v(2.72, -50.55) * mm});
            skLineSegment(sketch, "E131", {"start": v(2.72, -50.55) * mm, "end": v(3.04, -53.24) * mm});
            skLineSegment(sketch, "E132", {"start": v(3.04, -53.24) * mm, "end": v(3, -56.1) * mm});
            skLineSegment(sketch, "E133", {"start": v(3, -56.1) * mm, "end": v(2.97, -56.38) * mm});
            skLineSegment(sketch, "E134", {"start": v(2.53, -45.9) * mm, "end": v(1.25, -45.88) * mm});
            skLineSegment(sketch, "E135", {"start": v(1.25, -45.88) * mm, "end": v(1.02, -45.76) * mm});
            skLineSegment(sketch, "E136", {"start": v(1.02, -45.76) * mm, "end": v(1.21, -45.5) * mm});
            skLineSegment(sketch, "E137", {"start": v(1.21, -45.5) * mm, "end": v(1.56, -45.39) * mm});
            skLineSegment(sketch, "E138", {"start": v(1.56, -45.39) * mm, "end": v(2.1, -44.86) * mm});
            skLineSegment(sketch, "E139", {"start": v(2.1, -44.86) * mm, "end": v(2.2, -44.12) * mm});
            skLineSegment(sketch, "E140", {"start": v(2.2, -44.12) * mm, "end": v(1.76, -43.57) * mm});
            skLineSegment(sketch, "E141", {"start": v(1.76, -43.57) * mm, "end": v(1.18, -43.49) * mm});
            skLineSegment(sketch, "E142", {"start": v(1.18, -43.49) * mm, "end": v(0.67, -44.12) * mm});
            skLineSegment(sketch, "E143", {"start": v(0.67, -44.12) * mm, "end": v(0.5, -44.72) * mm});
            skLineSegment(sketch, "E144", {"start": v(0.5, -44.72) * mm, "end": v(-0.14, -45.7) * mm});
            skLineSegment(sketch, "E145", {"start": v(-0.14, -45.7) * mm, "end": v(-1.06, -45.96) * mm});
            skLineSegment(sketch, "E146", {"start": v(-1.06, -45.96) * mm, "end": v(-2.34, -45.32) * mm});
            skLineSegment(sketch, "E147", {"start": v(-2.34, -45.32) * mm, "end": v(-2.62, -44.47) * mm});
            skLineSegment(sketch, "E148", {"start": v(-2.62, -44.47) * mm, "end": v(-2.43, -43.9) * mm});
            skLineSegment(sketch, "E149", {"start": v(-2.43, -43.9) * mm, "end": v(-2.41, -43.53) * mm});
            skLineSegment(sketch, "E150", {"start": v(-2.41, -43.53) * mm, "end": v(-2.52, -43.2) * mm});
            skLineSegment(sketch, "E151", {"start": v(-2.52, -43.2) * mm, "end": v(-2.24, -43.08) * mm});
            skLineSegment(sketch, "E152", {"start": v(-2.24, -43.08) * mm, "end": v(-1.4, -43.06) * mm});
            skLineSegment(sketch, "E153", {"start": v(-1.4, -43.06) * mm, "end": v(-1.13, -43.14) * mm});
            skLineSegment(sketch, "E154", {"start": v(-1.13, -43.14) * mm, "end": v(-1.2, -43.4) * mm});
            skLineSegment(sketch, "E155", {"start": v(-1.2, -43.4) * mm, "end": v(-2.04, -43.98) * mm});
            skLineSegment(sketch, "E156", {"start": v(-2.04, -43.98) * mm, "end": v(-2.25, -44.48) * mm});
            skLineSegment(sketch, "E157", {"start": v(-2.25, -44.48) * mm, "end": v(-2.1, -45) * mm});
            skLineSegment(sketch, "E158", {"start": v(-2.1, -45) * mm, "end": v(-1.26, -45.23) * mm});
            skLineSegment(sketch, "E159", {"start": v(-1.26, -45.23) * mm, "end": v(-1.01, -44.83) * mm});
            skLineSegment(sketch, "E160", {"start": v(-1.01, -44.83) * mm, "end": v(-0.6, -43.64) * mm});
            skLineSegment(sketch, "E161", {"start": v(-0.6, -43.64) * mm, "end": v(0.07, -42.96) * mm});
            skLineSegment(sketch, "E162", {"start": v(0.07, -42.96) * mm, "end": v(1.04, -42.82) * mm});
            skLineSegment(sketch, "E163", {"start": v(1.04, -42.82) * mm, "end": v(1.96, -43.17) * mm});
            skLineSegment(sketch, "E164", {"start": v(1.96, -43.17) * mm, "end": v(2.6, -44.3) * mm});
            skLineSegment(sketch, "E165", {"start": v(2.6, -44.3) * mm, "end": v(2.42, -45) * mm});
            skLineSegment(sketch, "E166", {"start": v(2.42, -45) * mm, "end": v(2.36, -45.36) * mm});
            skLineSegment(sketch, "E167", {"start": v(2.36, -45.36) * mm, "end": v(2.61, -45.8) * mm});
            skLineSegment(sketch, "E168", {"start": v(2.61, -45.8) * mm, "end": v(2.53, -45.9) * mm});
            skLineSegment(sketch, "E169", {"start": v(2.45, -20.53) * mm, "end": v(1.13, -21.8) * mm});
            skLineSegment(sketch, "E170", {"start": v(1.13, -21.8) * mm, "end": v(-0.37, -21.99) * mm});
            skLineSegment(sketch, "E171", {"start": v(-0.37, -21.99) * mm, "end": v(-1.77, -21.4) * mm});
            skLineSegment(sketch, "E172", {"start": v(-1.77, -21.4) * mm, "end": v(-2.55, -20.32) * mm});
            skLineSegment(sketch, "E173", {"start": v(-2.55, -20.32) * mm, "end": v(-2.49, -19.2) * mm});
            skLineSegment(sketch, "E174", {"start": v(-2.49, -19.2) * mm, "end": v(-1.62, -18.06) * mm});
            skLineSegment(sketch, "E175", {"start": v(-1.62, -18.06) * mm, "end": v(-0.1, -17.66) * mm});
            skLineSegment(sketch, "E176", {"start": v(-0.1, -17.66) * mm, "end": v(1.4, -17.95) * mm});
            skLineSegment(sketch, "E177", {"start": v(1.4, -17.95) * mm, "end": v(2.31, -18.83) * mm});
            skLineSegment(sketch, "E178", {"start": v(2.31, -18.83) * mm, "end": v(2.59, -20.05) * mm});
            skLineSegment(sketch, "E179", {"start": v(2.59, -20.05) * mm, "end": v(2.45, -20.53) * mm});
            skLineSegment(sketch, "E180", {"start": v(2.03, -19.35) * mm, "end": v(1.73, -19.16) * mm});
            skLineSegment(sketch, "E181", {"start": v(1.73, -19.16) * mm, "end": v(0.89, -19.11) * mm});
            skLineSegment(sketch, "E182", {"start": v(0.89, -19.11) * mm, "end": v(-1.2, -19.12) * mm});
            skLineSegment(sketch, "E183", {"start": v(-1.2, -19.12) * mm, "end": v(-1.86, -19.19) * mm});
            skLineSegment(sketch, "E184", {"start": v(-1.86, -19.19) * mm, "end": v(-2.16, -19.48) * mm});
            skLineSegment(sketch, "E185", {"start": v(-2.16, -19.48) * mm, "end": v(-2.24, -19.96) * mm});
            skLineSegment(sketch, "E186", {"start": v(-2.24, -19.96) * mm, "end": v(-1.95, -20.39) * mm});
            skLineSegment(sketch, "E187", {"start": v(-1.95, -20.39) * mm, "end": v(-1.43, -20.52) * mm});
            skLineSegment(sketch, "E188", {"start": v(-1.43, -20.52) * mm, "end": v(0.1, -20.57) * mm});
            skLineSegment(sketch, "E189", {"start": v(0.1, -20.57) * mm, "end": v(1.58, -20.49) * mm});
            skLineSegment(sketch, "E190", {"start": v(1.58, -20.49) * mm, "end": v(2.1, -20.26) * mm});
            skLineSegment(sketch, "E191", {"start": v(2.1, -20.26) * mm, "end": v(2.18, -19.57) * mm});
            skLineSegment(sketch, "E192", {"start": v(2.18, -19.57) * mm, "end": v(2.03, -19.35) * mm});
            skLineSegment(sketch, "E193", {"start": v(0.52, -15.07) * mm, "end": v(-1.6, -16.42) * mm});
            skLineSegment(sketch, "E194", {"start": v(-1.6, -16.42) * mm, "end": v(0.92, -16.46) * mm});
            skLineSegment(sketch, "E195", {"start": v(0.92, -16.46) * mm, "end": v(2.01, -16.44) * mm});
            skLineSegment(sketch, "E196", {"start": v(2.01, -16.44) * mm, "end": v(2.15, -16.25) * mm});
            skLineSegment(sketch, "E197", {"start": v(2.15, -16.25) * mm, "end": v(2.2, -15.85) * mm});
            skLineSegment(sketch, "E198", {"start": v(2.2, -15.85) * mm, "end": v(2.45, -15.8) * mm});
            skLineSegment(sketch, "E199", {"start": v(2.45, -15.8) * mm, "end": v(2.52, -16.06) * mm});
            skLineSegment(sketch, "E200", {"start": v(2.52, -16.06) * mm, "end": v(2.49, -17.03) * mm});
            skLineSegment(sketch, "E201", {"start": v(2.49, -17.03) * mm, "end": v(2.4, -17.37) * mm});
            skLineSegment(sketch, "E202", {"start": v(2.4, -17.37) * mm, "end": v(2.2, -17.25) * mm});
            skLineSegment(sketch, "E203", {"start": v(2.2, -17.25) * mm, "end": v(2.15, -16.86) * mm});
            skLineSegment(sketch, "E204", {"start": v(2.15, -16.86) * mm, "end": v(-2.2, -16.86) * mm});
            skLineSegment(sketch, "E205", {"start": v(-2.2, -16.86) * mm, "end": v(-2.2, -17.31) * mm});
            skLineSegment(sketch, "E206", {"start": v(-2.2, -17.31) * mm, "end": v(-2.41, -17.45) * mm});
            skLineSegment(sketch, "E207", {"start": v(-2.41, -17.45) * mm, "end": v(-2.54, -17.26) * mm});
            skLineSegment(sketch, "E208", {"start": v(-2.54, -17.26) * mm, "end": v(-2.53, -16.3) * mm});
            skLineSegment(sketch, "E209", {"start": v(-2.53, -16.3) * mm, "end": v(-2.51, -15.55) * mm});
            skLineSegment(sketch, "E210", {"start": v(-2.51, -15.55) * mm, "end": v(-0.05, -13.93) * mm});
            skLineSegment(sketch, "E211", {"start": v(-0.05, -13.93) * mm, "end": v(0.13, -13.78) * mm});
            skLineSegment(sketch, "E212", {"start": v(0.13, -13.78) * mm, "end": v(-0.45, -13.75) * mm});
            skLineSegment(sketch, "E213", {"start": v(-0.45, -13.75) * mm, "end": v(-2.05, -13.78) * mm});
            skLineSegment(sketch, "E214", {"start": v(-2.05, -13.78) * mm, "end": v(-2.15, -13.79) * mm});
            skLineSegment(sketch, "E215", {"start": v(-2.15, -13.79) * mm, "end": v(-2.23, -14.21) * mm});
            skLineSegment(sketch, "E216", {"start": v(-2.23, -14.21) * mm, "end": v(-2.43, -14.35) * mm});
            skLineSegment(sketch, "E217", {"start": v(-2.43, -14.35) * mm, "end": v(-2.5, -14.07) * mm});
            skLineSegment(sketch, "E218", {"start": v(-2.5, -14.07) * mm, "end": v(-2.5, -13.1) * mm});
            skLineSegment(sketch, "E219", {"start": v(-2.5, -13.1) * mm, "end": v(-2.43, -12.83) * mm});
            skLineSegment(sketch, "E220", {"start": v(-2.43, -12.83) * mm, "end": v(-2.23, -12.97) * mm});
            skLineSegment(sketch, "E221", {"start": v(-2.23, -12.97) * mm, "end": v(-2.11, -13.3) * mm});
            skLineSegment(sketch, "E222", {"start": v(-2.11, -13.3) * mm, "end": v(-1.65, -13.41) * mm});
            skLineSegment(sketch, "E223", {"start": v(-1.65, -13.41) * mm, "end": v(1.6, -13.44) * mm});
            skLineSegment(sketch, "E224", {"start": v(1.6, -13.44) * mm, "end": v(2.47, -13.48) * mm});
            skLineSegment(sketch, "E225", {"start": v(2.47, -13.48) * mm, "end": v(2.56, -13.64) * mm});
            skLineSegment(sketch, "E226", {"start": v(2.56, -13.64) * mm, "end": v(1.88, -14.16) * mm});
            skLineSegment(sketch, "E227", {"start": v(1.88, -14.16) * mm, "end": v(0.52, -15.07) * mm});
            skLineSegment(sketch, "E228", {"start": v(18.94, -0.4) * mm, "end": v(18.94, -0.4) * mm});
            skLineSegment(sketch, "E229", {"start": v(2.44, -41.54) * mm, "end": v(2.22, -41.47) * mm});
            skLineSegment(sketch, "E230", {"start": v(2.22, -41.47) * mm, "end": v(2.17, -40.9) * mm});
            skLineSegment(sketch, "E231", {"start": v(2.17, -40.9) * mm, "end": v(2.15, -40.8) * mm});
            skLineSegment(sketch, "E232", {"start": v(2.15, -40.8) * mm, "end": v(0.26, -40.8) * mm});
            skLineSegment(sketch, "E233", {"start": v(0.26, -40.8) * mm, "end": v(-1.38, -41.7) * mm});
            skLineSegment(sketch, "E234", {"start": v(-1.38, -41.7) * mm, "end": v(-2.1, -42.16) * mm});
            skLineSegment(sketch, "E235", {"start": v(-2.1, -42.16) * mm, "end": v(-2.25, -42.43) * mm});
            skLineSegment(sketch, "E236", {"start": v(-2.25, -42.43) * mm, "end": v(-2.47, -42.42) * mm});
            skLineSegment(sketch, "E237", {"start": v(-2.47, -42.42) * mm, "end": v(-2.53, -41.76) * mm});
            skLineSegment(sketch, "E238", {"start": v(-2.53, -41.76) * mm, "end": v(-2.55, -40.53) * mm});
            skLineSegment(sketch, "E239", {"start": v(-2.55, -40.53) * mm, "end": v(-2.48, -40.25) * mm});
            skLineSegment(sketch, "E240", {"start": v(-2.48, -40.25) * mm, "end": v(-2.21, -40.33) * mm});
            skLineSegment(sketch, "E241", {"start": v(-2.21, -40.33) * mm, "end": v(-2.14, -40.58) * mm});
            skLineSegment(sketch, "E242", {"start": v(-2.14, -40.58) * mm, "end": v(-1.87, -40.52) * mm});
            skLineSegment(sketch, "E243", {"start": v(-1.87, -40.52) * mm, "end": v(-0.7, -39.94) * mm});
            skLineSegment(sketch, "E244", {"start": v(-0.7, -39.94) * mm, "end": v(-0.26, -39.72) * mm});
            skLineSegment(sketch, "E245", {"start": v(-0.26, -39.72) * mm, "end": v(-1.96, -38.91) * mm});
            skLineSegment(sketch, "E246", {"start": v(-1.96, -38.91) * mm, "end": v(-2.17, -38.9) * mm});
            skLineSegment(sketch, "E247", {"start": v(-2.17, -38.9) * mm, "end": v(-2.27, -39.22) * mm});
            skLineSegment(sketch, "E248", {"start": v(-2.27, -39.22) * mm, "end": v(-2.5, -39.2) * mm});
            skLineSegment(sketch, "E249", {"start": v(-2.5, -39.2) * mm, "end": v(-2.56, -38.8) * mm});
            skLineSegment(sketch, "E250", {"start": v(-2.56, -38.8) * mm, "end": v(-2.54, -38.12) * mm});
            skLineSegment(sketch, "E251", {"start": v(-2.54, -38.12) * mm, "end": v(-2.37, -37.97) * mm});
            skLineSegment(sketch, "E252", {"start": v(-2.37, -37.97) * mm, "end": v(-2.15, -38.23) * mm});
            skLineSegment(sketch, "E253", {"start": v(-2.15, -38.23) * mm, "end": v(-1.8, -38.55) * mm});
            skLineSegment(sketch, "E254", {"start": v(-1.8, -38.55) * mm, "end": v(-0.46, -39.25) * mm});
            skLineSegment(sketch, "E255", {"start": v(-0.46, -39.25) * mm, "end": v(0.12, -39.54) * mm});
            skLineSegment(sketch, "E256", {"start": v(0.12, -39.54) * mm, "end": v(2.15, -39.54) * mm});
            skLineSegment(sketch, "E257", {"start": v(2.15, -39.54) * mm, "end": v(2.2, -39) * mm});
            skLineSegment(sketch, "E258", {"start": v(2.2, -39) * mm, "end": v(2.39, -38.81) * mm});
            skLineSegment(sketch, "E259", {"start": v(2.39, -38.81) * mm, "end": v(2.47, -39.1) * mm});
            skLineSegment(sketch, "E260", {"start": v(2.47, -39.1) * mm, "end": v(2.51, -40.4) * mm});
            skLineSegment(sketch, "E261", {"start": v(2.51, -40.4) * mm, "end": v(2.48, -41.43) * mm});
            skLineSegment(sketch, "E262", {"start": v(2.48, -41.43) * mm, "end": v(2.44, -41.54) * mm});
            skLineSegment(sketch, "E263", {"start": v(2.37, -37.86) * mm, "end": v(2.17, -37.55) * mm});
            skLineSegment(sketch, "E264", {"start": v(2.17, -37.55) * mm, "end": v(2.12, -37.24) * mm});
            skLineSegment(sketch, "E265", {"start": v(2.12, -37.24) * mm, "end": v(-2.18, -37.19) * mm});
            skLineSegment(sketch, "E266", {"start": v(-2.18, -37.19) * mm, "end": v(-2.24, -37.66) * mm});
            skLineSegment(sketch, "E267", {"start": v(-2.24, -37.66) * mm, "end": v(-2.42, -37.8) * mm});
            skLineSegment(sketch, "E268", {"start": v(-2.42, -37.8) * mm, "end": v(-2.5, -37.53) * mm});
            skLineSegment(sketch, "E269", {"start": v(-2.5, -37.53) * mm, "end": v(-2.55, -36.23) * mm});
            skLineSegment(sketch, "E270", {"start": v(-2.55, -36.23) * mm, "end": v(-2.56, -35.75) * mm});
            skLineSegment(sketch, "E271", {"start": v(-2.56, -35.75) * mm, "end": v(-0.48, -35.14) * mm});
            skLineSegment(sketch, "E272", {"start": v(-0.48, -35.14) * mm, "end": v(-0.02, -34.96) * mm});
            skLineSegment(sketch, "E273", {"start": v(-0.02, -34.96) * mm, "end": v(-0.17, -34.8) * mm});
            skLineSegment(sketch, "E274", {"start": v(-0.17, -34.8) * mm, "end": v(-1.17, -34.48) * mm});
            skLineSegment(sketch, "E275", {"start": v(-1.17, -34.48) * mm, "end": v(-2.56, -34.06) * mm});
            skLineSegment(sketch, "E276", {"start": v(-2.56, -34.06) * mm, "end": v(-2.55, -32.52) * mm});
            skLineSegment(sketch, "E277", {"start": v(-2.55, -32.52) * mm, "end": v(-2.5, -32.15) * mm});
            skLineSegment(sketch, "E278", {"start": v(-2.5, -32.15) * mm, "end": v(-2.26, -32.14) * mm});
            skLineSegment(sketch, "E279", {"start": v(-2.26, -32.14) * mm, "end": v(-2.2, -32.45) * mm});
            skLineSegment(sketch, "E280", {"start": v(-2.2, -32.45) * mm, "end": v(-2.2, -32.7) * mm});
            skLineSegment(sketch, "E281", {"start": v(-2.2, -32.7) * mm, "end": v(2.17, -32.7) * mm});
            skLineSegment(sketch, "E282", {"start": v(2.17, -32.7) * mm, "end": v(2.18, -32.25) * mm});
            skLineSegment(sketch, "E283", {"start": v(2.18, -32.25) * mm, "end": v(2.38, -32.1) * mm});
            skLineSegment(sketch, "E284", {"start": v(2.38, -32.1) * mm, "end": v(2.5, -32.32) * mm});
            skLineSegment(sketch, "E285", {"start": v(2.5, -32.32) * mm, "end": v(2.5, -33.37) * mm});
            skLineSegment(sketch, "E286", {"start": v(2.5, -33.37) * mm, "end": v(2.46, -34.41) * mm});
            skLineSegment(sketch, "E287", {"start": v(2.46, -34.41) * mm, "end": v(2.3, -34.59) * mm});
            skLineSegment(sketch, "E288", {"start": v(2.3, -34.59) * mm, "end": v(2.18, -34.27) * mm});
            skLineSegment(sketch, "E289", {"start": v(2.18, -34.27) * mm, "end": v(2.15, -33.97) * mm});
            skLineSegment(sketch, "E290", {"start": v(2.15, -33.97) * mm, "end": v(-0.57, -33.99) * mm});
            skLineSegment(sketch, "E291", {"start": v(-0.57, -33.99) * mm, "end": v(-1.5, -34.02) * mm});
            skLineSegment(sketch, "E292", {"start": v(-1.5, -34.02) * mm, "end": v(-1.34, -34.07) * mm});
            skLineSegment(sketch, "E293", {"start": v(-1.34, -34.07) * mm, "end": v(1.13, -34.85) * mm});
            skLineSegment(sketch, "E294", {"start": v(1.13, -34.85) * mm, "end": v(2.42, -35.32) * mm});
            skLineSegment(sketch, "E295", {"start": v(2.42, -35.32) * mm, "end": v(2.47, -35.44) * mm});
            skLineSegment(sketch, "E296", {"start": v(2.47, -35.44) * mm, "end": v(1.67, -35.76) * mm});
            skLineSegment(sketch, "E297", {"start": v(1.67, -35.76) * mm, "end": v(-0.06, -36.3) * mm});
            skLineSegment(sketch, "E298", {"start": v(-0.06, -36.3) * mm, "end": v(-1.6, -36.79) * mm});
            skLineSegment(sketch, "E299", {"start": v(-1.6, -36.79) * mm, "end": v(2.12, -36.75) * mm});
            skLineSegment(sketch, "E300", {"start": v(2.12, -36.75) * mm, "end": v(2.2, -36.33) * mm});
            skLineSegment(sketch, "E301", {"start": v(2.2, -36.33) * mm, "end": v(2.4, -36.19) * mm});
            skLineSegment(sketch, "E302", {"start": v(2.4, -36.19) * mm, "end": v(2.48, -36.5) * mm});
            skLineSegment(sketch, "E303", {"start": v(2.48, -36.5) * mm, "end": v(2.52, -37.55) * mm});
            skLineSegment(sketch, "E304", {"start": v(2.52, -37.55) * mm, "end": v(2.48, -37.84) * mm});
            skLineSegment(sketch, "E305", {"start": v(2.48, -37.84) * mm, "end": v(2.37, -37.86) * mm});
            skLineSegment(sketch, "E306", {"start": v(-3.85, -2.27) * mm, "end": v(-3.85, -2.27) * mm});
            skLineSegment(sketch, "E307", {"start": v(2.44, -31.96) * mm, "end": v(2.22, -31.9) * mm});
            skLineSegment(sketch, "E308", {"start": v(2.22, -31.9) * mm, "end": v(2.17, -31.41) * mm});
            skLineSegment(sketch, "E309", {"start": v(2.17, -31.41) * mm, "end": v(2.1, -31.38) * mm});
            skLineSegment(sketch, "E310", {"start": v(2.1, -31.38) * mm, "end": v(-2.15, -31.38) * mm});
            skLineSegment(sketch, "E311", {"start": v(-2.15, -31.38) * mm, "end": v(-2.23, -31.8) * mm});
            skLineSegment(sketch, "E312", {"start": v(-2.23, -31.8) * mm, "end": v(-2.42, -31.94) * mm});
            skLineSegment(sketch, "E313", {"start": v(-2.42, -31.94) * mm, "end": v(-2.5, -31.6) * mm});
            skLineSegment(sketch, "E314", {"start": v(-2.5, -31.6) * mm, "end": v(-2.51, -30.05) * mm});
            skLineSegment(sketch, "E315", {"start": v(-2.51, -30.05) * mm, "end": v(-2.43, -28.78) * mm});
            skLineSegment(sketch, "E316", {"start": v(-2.43, -28.78) * mm, "end": v(-2.07, -28.14) * mm});
            skLineSegment(sketch, "E317", {"start": v(-2.07, -28.14) * mm, "end": v(-1.47, -27.81) * mm});
            skLineSegment(sketch, "E318", {"start": v(-1.47, -27.81) * mm, "end": v(-0.53, -27.96) * mm});
            skLineSegment(sketch, "E319", {"start": v(-0.53, -27.96) * mm, "end": v(0.12, -29.05) * mm});
            skLineSegment(sketch, "E320", {"start": v(0.12, -29.05) * mm, "end": v(0.17, -30) * mm});
            skLineSegment(sketch, "E321", {"start": v(0.17, -30) * mm, "end": v(0.22, -30.05) * mm});
            skLineSegment(sketch, "E322", {"start": v(0.22, -30.05) * mm, "end": v(2.16, -30.1) * mm});
            skLineSegment(sketch, "E323", {"start": v(2.16, -30.1) * mm, "end": v(2.2, -29.6) * mm});
            skLineSegment(sketch, "E324", {"start": v(2.2, -29.6) * mm, "end": v(2.4, -29.44) * mm});
            skLineSegment(sketch, "E325", {"start": v(2.4, -29.44) * mm, "end": v(2.47, -29.75) * mm});
            skLineSegment(sketch, "E326", {"start": v(2.47, -29.75) * mm, "end": v(2.51, -31.08) * mm});
            skLineSegment(sketch, "E327", {"start": v(2.51, -31.08) * mm, "end": v(2.47, -31.87) * mm});
            skLineSegment(sketch, "E328", {"start": v(2.47, -31.87) * mm, "end": v(2.44, -31.96) * mm});
            skLineSegment(sketch, "E329", {"start": v(-0.33, -29.29) * mm, "end": v(-0.76, -29.13) * mm});
            skLineSegment(sketch, "E330", {"start": v(-0.76, -29.13) * mm, "end": v(-1.7, -29.15) * mm});
            skLineSegment(sketch, "E331", {"start": v(-1.7, -29.15) * mm, "end": v(-2.16, -29.53) * mm});
            skLineSegment(sketch, "E332", {"start": v(-2.16, -29.53) * mm, "end": v(-2.2, -30.04) * mm});
            skLineSegment(sketch, "E333", {"start": v(-2.2, -30.04) * mm, "end": v(-2.11, -30.06) * mm});
            skLineSegment(sketch, "E334", {"start": v(-2.11, -30.06) * mm, "end": v(-0.08, -30.06) * mm});
            skLineSegment(sketch, "E335", {"start": v(-0.08, -30.06) * mm, "end": v(-0.3, -29.32) * mm});
            skLineSegment(sketch, "E336", {"start": v(-0.3, -29.32) * mm, "end": v(-0.33, -29.29) * mm});
            skLineSegment(sketch, "E337", {"start": v(4.72, 0.43) * mm, "end": v(4.72, 0.43) * mm});
            skLineSegment(sketch, "E338", {"start": v(2.35, -27.52) * mm, "end": v(2.17, -27.35) * mm});
            skLineSegment(sketch, "E339", {"start": v(2.17, -27.35) * mm, "end": v(2.17, -26.93) * mm});
            skLineSegment(sketch, "E340", {"start": v(2.17, -26.93) * mm, "end": v(-2.2, -26.93) * mm});
            skLineSegment(sketch, "E341", {"start": v(-2.2, -26.93) * mm, "end": v(-2.2, -27.38) * mm});
            skLineSegment(sketch, "E342", {"start": v(-2.2, -27.38) * mm, "end": v(-2.4, -27.51) * mm});
            skLineSegment(sketch, "E343", {"start": v(-2.4, -27.51) * mm, "end": v(-2.54, -27.3) * mm});
            skLineSegment(sketch, "E344", {"start": v(-2.54, -27.3) * mm, "end": v(-2.56, -26.25) * mm});
            skLineSegment(sketch, "E345", {"start": v(-2.56, -26.25) * mm, "end": v(-2.53, -25.27) * mm});
            skLineSegment(sketch, "E346", {"start": v(-2.53, -25.27) * mm, "end": v(-2.4, -25.07) * mm});
            skLineSegment(sketch, "E347", {"start": v(-2.4, -25.07) * mm, "end": v(-2.2, -25.22) * mm});
            skLineSegment(sketch, "E348", {"start": v(-2.2, -25.22) * mm, "end": v(-2.2, -25.66) * mm});
            skLineSegment(sketch, "E349", {"start": v(-2.2, -25.66) * mm, "end": v(-0.29, -25.66) * mm});
            skLineSegment(sketch, "E350", {"start": v(-0.29, -25.66) * mm, "end": v(-0.29, -24.2) * mm});
            skLineSegment(sketch, "E351", {"start": v(-0.29, -24.2) * mm, "end": v(-2.2, -24.2) * mm});
            skLineSegment(sketch, "E352", {"start": v(-2.2, -24.2) * mm, "end": v(-2.2, -24.64) * mm});
            skLineSegment(sketch, "E353", {"start": v(-2.2, -24.64) * mm, "end": v(-2.4, -24.78) * mm});
            skLineSegment(sketch, "E354", {"start": v(-2.4, -24.78) * mm, "end": v(-2.54, -24.57) * mm});
            skLineSegment(sketch, "E355", {"start": v(-2.54, -24.57) * mm, "end": v(-2.56, -23.52) * mm});
            skLineSegment(sketch, "E356", {"start": v(-2.56, -23.52) * mm, "end": v(-2.53, -22.53) * mm});
            skLineSegment(sketch, "E357", {"start": v(-2.53, -22.53) * mm, "end": v(-2.4, -22.34) * mm});
            skLineSegment(sketch, "E358", {"start": v(-2.4, -22.34) * mm, "end": v(-2.2, -22.49) * mm});
            skLineSegment(sketch, "E359", {"start": v(-2.2, -22.49) * mm, "end": v(-2.2, -22.92) * mm});
            skLineSegment(sketch, "E360", {"start": v(-2.2, -22.92) * mm, "end": v(2.17, -22.92) * mm});
            skLineSegment(sketch, "E361", {"start": v(2.17, -22.92) * mm, "end": v(2.18, -22.47) * mm});
            skLineSegment(sketch, "E362", {"start": v(2.18, -22.47) * mm, "end": v(2.38, -22.34) * mm});
            skLineSegment(sketch, "E363", {"start": v(2.38, -22.34) * mm, "end": v(2.5, -22.55) * mm});
            skLineSegment(sketch, "E364", {"start": v(2.5, -22.55) * mm, "end": v(2.53, -23.6) * mm});
            skLineSegment(sketch, "E365", {"start": v(2.53, -23.6) * mm, "end": v(2.5, -24.59) * mm});
            skLineSegment(sketch, "E366", {"start": v(2.5, -24.59) * mm, "end": v(2.36, -24.78) * mm});
            skLineSegment(sketch, "E367", {"start": v(2.36, -24.78) * mm, "end": v(2.17, -24.63) * mm});
            skLineSegment(sketch, "E368", {"start": v(2.17, -24.63) * mm, "end": v(2.17, -24.2) * mm});
            skLineSegment(sketch, "E369", {"start": v(2.17, -24.2) * mm, "end": v(0.08, -24.2) * mm});
            skLineSegment(sketch, "E370", {"start": v(0.08, -24.2) * mm, "end": v(0.08, -25.66) * mm});
            skLineSegment(sketch, "E371", {"start": v(0.08, -25.66) * mm, "end": v(2.17, -25.66) * mm});
            skLineSegment(sketch, "E372", {"start": v(2.17, -25.66) * mm, "end": v(2.18, -25.2) * mm});
            skLineSegment(sketch, "E373", {"start": v(2.18, -25.2) * mm, "end": v(2.38, -25.07) * mm});
            skLineSegment(sketch, "E374", {"start": v(2.38, -25.07) * mm, "end": v(2.5, -25.28) * mm});
            skLineSegment(sketch, "E375", {"start": v(2.5, -25.28) * mm, "end": v(2.53, -26.33) * mm});
            skLineSegment(sketch, "E376", {"start": v(2.53, -26.33) * mm, "end": v(2.5, -27.32) * mm});
            skLineSegment(sketch, "E377", {"start": v(2.5, -27.32) * mm, "end": v(2.36, -27.52) * mm});
            skLineSegment(sketch, "E378", {"start": v(2.36, -27.52) * mm, "end": v(2.35, -27.52) * mm});
            skLineSegment(sketch, "E379", {"start": v(6.5, -2.24) * mm, "end": v(6.5, -2.24) * mm});
            skLineSegment(sketch, "E380", {"start": v(2.48, -11.7) * mm, "end": v(2.24, -11.64) * mm});
            skLineSegment(sketch, "E381", {"start": v(2.24, -11.64) * mm, "end": v(2.17, -11.09) * mm});
            skLineSegment(sketch, "E382", {"start": v(2.17, -11.09) * mm, "end": v(2.15, -11) * mm});
            skLineSegment(sketch, "E383", {"start": v(2.15, -11) * mm, "end": v(0.26, -11) * mm});
            skLineSegment(sketch, "E384", {"start": v(0.26, -11) * mm, "end": v(-1.38, -11.88) * mm});
            skLineSegment(sketch, "E385", {"start": v(-1.38, -11.88) * mm, "end": v(-2.1, -12.36) * mm});
            skLineSegment(sketch, "E386", {"start": v(-2.1, -12.36) * mm, "end": v(-2.23, -12.6) * mm});
            skLineSegment(sketch, "E387", {"start": v(-2.23, -12.6) * mm, "end": v(-2.5, -12.63) * mm});
            skLineSegment(sketch, "E388", {"start": v(-2.5, -12.63) * mm, "end": v(-2.55, -12.3) * mm});
            skLineSegment(sketch, "E389", {"start": v(-2.55, -12.3) * mm, "end": v(-2.52, -10.94) * mm});
            skLineSegment(sketch, "E390", {"start": v(-2.52, -10.94) * mm, "end": v(-2.45, -10.43) * mm});
            skLineSegment(sketch, "E391", {"start": v(-2.45, -10.43) * mm, "end": v(-2.25, -10.48) * mm});
            skLineSegment(sketch, "E392", {"start": v(-2.25, -10.48) * mm, "end": v(-2.15, -10.84) * mm});
            skLineSegment(sketch, "E393", {"start": v(-2.15, -10.84) * mm, "end": v(-2.09, -10.83) * mm});
            skLineSegment(sketch, "E394", {"start": v(-2.09, -10.83) * mm, "end": v(-0.27, -9.87) * mm});
            skLineSegment(sketch, "E395", {"start": v(-0.27, -9.87) * mm, "end": v(-1.91, -9.12) * mm});
            skLineSegment(sketch, "E396", {"start": v(-1.91, -9.12) * mm, "end": v(-2.16, -9.08) * mm});
            skLineSegment(sketch, "E397", {"start": v(-2.16, -9.08) * mm, "end": v(-2.25, -9.4) * mm});
            skLineSegment(sketch, "E398", {"start": v(-2.25, -9.4) * mm, "end": v(-2.5, -9.4) * mm});
            skLineSegment(sketch, "E399", {"start": v(-2.5, -9.4) * mm, "end": v(-2.56, -9.05) * mm});
            skLineSegment(sketch, "E400", {"start": v(-2.56, -9.05) * mm, "end": v(-2.54, -8.25) * mm});
            skLineSegment(sketch, "E401", {"start": v(-2.54, -8.25) * mm, "end": v(-2.4, -8.07) * mm});
            skLineSegment(sketch, "E402", {"start": v(-2.4, -8.07) * mm, "end": v(-2.2, -8.24) * mm});
            skLineSegment(sketch, "E403", {"start": v(-2.2, -8.24) * mm, "end": v(-2, -8.58) * mm});
            skLineSegment(sketch, "E404", {"start": v(-2, -8.58) * mm, "end": v(-1.16, -9.07) * mm});
            skLineSegment(sketch, "E405", {"start": v(-1.16, -9.07) * mm, "end": v(0.16, -9.73) * mm});
            skLineSegment(sketch, "E406", {"start": v(0.16, -9.73) * mm, "end": v(2.15, -9.73) * mm});
            skLineSegment(sketch, "E407", {"start": v(2.15, -9.73) * mm, "end": v(2.2, -9.19) * mm});
            skLineSegment(sketch, "E408", {"start": v(2.2, -9.19) * mm, "end": v(2.39, -9) * mm});
            skLineSegment(sketch, "E409", {"start": v(2.39, -9) * mm, "end": v(2.47, -9.28) * mm});
            skLineSegment(sketch, "E410", {"start": v(2.47, -9.28) * mm, "end": v(2.51, -10.59) * mm});
            skLineSegment(sketch, "E411", {"start": v(2.51, -10.59) * mm, "end": v(2.5, -11.65) * mm});
            skLineSegment(sketch, "E412", {"start": v(2.5, -11.65) * mm, "end": v(2.48, -11.7) * mm});
            skLineSegment(sketch, "E413", {"start": v(22.3, -2.37) * mm, "end": v(22.3, -2.37) * mm});
            skLineSegment(sketch, "E414", {"start": v(2.3, -56.1) * mm, "end": v(2.1, -57.03) * mm});
            skLineSegment(sketch, "E415", {"start": v(2.1, -57.03) * mm, "end": v(1.91, -57.44) * mm});
            skLineSegment(sketch, "E416", {"start": v(1.91, -57.44) * mm, "end": v(1.63, -57.38) * mm});
            skLineSegment(sketch, "E417", {"start": v(1.63, -57.38) * mm, "end": v(1.44, -56.9) * mm});
            skLineSegment(sketch, "E418", {"start": v(1.44, -56.9) * mm, "end": v(1.58, -56.97) * mm});
            skLineSegment(sketch, "E419", {"start": v(1.58, -56.97) * mm, "end": v(1.8, -57.08) * mm});
            skLineSegment(sketch, "E420", {"start": v(1.92, -56.53) * mm, "end": v(2.03, -54.1) * mm});
            skLineSegment(sketch, "E421", {"start": v(2.03, -54.1) * mm, "end": v(1.94, -51.74) * mm});
            skLineSegment(sketch, "E422", {"start": v(1.94, -51.74) * mm, "end": v(1.8, -51.17) * mm});
            skLineSegment(sketch, "E423", {"start": v(1.8, -51.17) * mm, "end": v(1.6, -51.14) * mm});
            skLineSegment(sketch, "E424", {"start": v(1.6, -51.14) * mm, "end": v(1.43, -51.13) * mm});
            skLineSegment(sketch, "E425", {"start": v(1.43, -51.13) * mm, "end": v(1.75, -50.71) * mm});
            skLineSegment(sketch, "E426", {"start": v(1.75, -50.71) * mm, "end": v(2, -50.86) * mm});
            skLineSegment(sketch, "E427", {"start": v(2, -50.86) * mm, "end": v(2.21, -51.64) * mm});
            skLineSegment(sketch, "E428", {"start": v(2.21, -51.64) * mm, "end": v(2.3, -53.64) * mm});
            skLineSegment(sketch, "E429", {"start": v(2.3, -53.64) * mm, "end": v(2.3, -55.95) * mm});
            skLineSegment(sketch, "E430", {"start": v(2.3, -55.95) * mm, "end": v(2.3, -56.1) * mm});
            skLineSegment(sketch, "E431", {"start": v(-22.1, -2.19) * mm, "end": v(-22.1, -2.19) * mm});
            skLineSegment(sketch, "E432", {"start": v(1.61, -54.73) * mm, "end": v(0.5, -55.97) * mm});
            skLineSegment(sketch, "E433", {"start": v(0.5, -55.97) * mm, "end": v(-0.66, -56.12) * mm});
            skLineSegment(sketch, "E434", {"start": v(-0.66, -56.12) * mm, "end": v(-1.58, -55.63) * mm});
            skLineSegment(sketch, "E435", {"start": v(-1.58, -55.63) * mm, "end": v(-2.78, -54.74) * mm});
            skLineSegment(sketch, "E436", {"start": v(-2.78, -54.74) * mm, "end": v(-3.46, -54.3) * mm});
            skLineSegment(sketch, "E437", {"start": v(-3.46, -54.3) * mm, "end": v(-3.74, -54.1) * mm});
            skLineSegment(sketch, "E438", {"start": v(-3.74, -54.1) * mm, "end": v(-3.52, -53.95) * mm});
            skLineSegment(sketch, "E439", {"start": v(-3.52, -53.95) * mm, "end": v(-2.92, -53.64) * mm});
            skLineSegment(sketch, "E440", {"start": v(-2.92, -53.64) * mm, "end": v(-1.78, -52.82) * mm});
            skLineSegment(sketch, "E441", {"start": v(-1.78, -52.82) * mm, "end": v(-0.73, -52.17) * mm});
            skLineSegment(sketch, "E442", {"start": v(-0.73, -52.17) * mm, "end": v(0, -52.11) * mm});
            skLineSegment(sketch, "E443", {"start": v(0, -52.11) * mm, "end": v(1.42, -53.12) * mm});
            skLineSegment(sketch, "E444", {"start": v(1.42, -53.12) * mm, "end": v(1.61, -54.73) * mm});
            skLineSegment(sketch, "E445", {"start": v(0.82, -57.34) * mm, "end": v(1.09, -57.02) * mm});
            skLineSegment(sketch, "E446", {"start": v(1.23, -50.84) * mm, "end": v(0.86, -50.95) * mm});
            skSolve(sketch);
        }
        {
            var Q0;
            Q0 = qSketchRegion(id + "F8", true);
            extrude(context, id + "F9", {"entities" : qUnion([Q0]), "operationType" : NewBodyOperationType.REMOVE, "oppositeDirection" : true, "depth" : 0.8 * mm, "offsetDistance" : 25 * mm});
        }
        {
            var Q0;
            {var subQ0=sQuery(id+"F1.wireOp",EDGE,"E39.left");var subQ1=sQuery(id+"F1.wireOp",EDGE,"E39.top");var subQ2=sQuery(id+"F1.wireOp",EDGE,"E39.right");var subQ3=sQuery(id+"F1.wireOp",EDGE,"E59.right");var subQ4=sQuery(id+"F1.wireOp",EDGE,"E59.top");var subQ5=sQuery(id+"F1.wireOp",EDGE,"E59.bottom");var subQ6=sQuery(id+"F1.wireOp",EDGE,"E46.left");var subQ7=sQuery(id+"F1.wireOp",EDGE,"E46.top");var subQ8=sQuery(id+"F1.wireOp",EDGE,"E46.right");var subQ9=sQuery(id+"F1.wireOp",EDGE,"E59.left");Q0=makeQuery(id+"F9.boolean.opBoolean","SPLIT",FACE,{"disambiguationData":[TD([makeQuery(id+"F2.opExtrude","SWEPT_FACE",FACE,{"disambiguationData":[OSD([subQ1])]})])],"derivedFrom":makeQuery(id+"F2.opExtrude","CAP_FACE",FACE,{"disambiguationData":[OSD([subQ1,subQ0,subQ2,sQuery(id+"F1.wireOp",EDGE,"E41"),sQuery(id+"F1.wireOp",EDGE,"E42.MirrorC"),sQuery(id+"F1.wireOp",EDGE,"E43.MirrorC"),sQuery(id+"F1.wireOp",EDGE,"E44.MirrorC"),subQ7,subQ6,subQ8,sQuery(id+"F1.wireOp",EDGE,"E47"),sQuery(id+"F1.wireOp",EDGE,"E50.MirrorC"),sQuery(id+"F1.wireOp",EDGE,"E52.MirrorC"),sQuery(id+"F1.wireOp",EDGE,"E55.MirrorC"),sQuery(id+"F1.wireOp",EDGE,"E56"),sQuery(id+"F1.wireOp",EDGE,"E57.1.0.0"),sQuery(id+"F1.wireOp",EDGE,"E57.2.0.0"),sQuery(id+"F1.wireOp",EDGE,"E57.3.0.0"),subQ5,subQ4,subQ9,subQ3])],"isStart":false})});}
            var sketch = newSketch(context, id + "F10", { "sketchPlane" : qUnion([Q0])});
            skCircle(sketch, "E447.0", {"center": v(19.65, -31.08) * mm, "radius": 5 * mm});
            skCircle(sketch, "E448.0", {"center": v(19.65, -31.08) * mm, "radius": 8.5 * mm});
            skSolve(sketch);
        }
        {
            var Q0;
            Q0=makeQuery(id+"F10.imprint","IMPRINT",FACE,{"disambiguationData":[TD([[makeQuery(id+"F10.imprint","IMPRINT",EDGE,{"derivedFrom":sQuery(id+"F10.wireOp",EDGE,"E447.0")}),1.0]])]});
            extrude(context, id + "F11", {"entities" : qUnion([Q0]), "operationType" : NewBodyOperationType.REMOVE, "oppositeDirection" : true, "depth" : (4 - 1.9) * mm, "offsetDistance" : 25 * mm});
        }
        {
            var Q0;
            Q0=makeQuery(id+"F10.imprint","IMPRINT",FACE,{"disambiguationData":[TD([[makeQuery(id+"F10.imprint","IMPRINT",EDGE,{"derivedFrom":sQuery(id+"F10.wireOp",EDGE,"E447.0")}),-1.0]])]});
            extrude(context, id + "F12", {"entities" : qUnion([Q0]), "operationType" : NewBodyOperationType.ADD, "depth" : 8 * mm, "offsetDistance" : 25 * mm});
        }
        {
            var Q0;
            Q0=makeQuery(id+"F10.imprint","IMPRINT",FACE,{"disambiguationData":[TD([[makeQuery(id+"F10.imprint","IMPRINT",EDGE,{"derivedFrom":sQuery(id+"F10.wireOp",EDGE,"E448.0")}),-1.0]])]});
            var sketch = newSketch(context, id + "F13", { "sketchPlane" : qUnion([Q0])});
            skLineSegment(sketch, "E449.bottom", {"start": v(-22.1, -38) * mm, "end": v(-15.9, -38) * mm});
            skLineSegment(sketch, "E449.top", {"start": v(-22.1, -44.8) * mm, "end": v(-15.9, -44.8) * mm});
            skLineSegment(sketch, "E449.left", {"start": v(-22.1, -38) * mm, "end": v(-22.1, -44.8) * mm});
            skLineSegment(sketch, "E449.right", {"start": v(-15.9, -38) * mm, "end": v(-15.9, -44.8) * mm});
            skPoint(sketch, "E450.0", {"position": v(-19, -12.5) * mm});
            skPoint(sketch, "E451.0", {"position": v(-19, -57.5) * mm});
            skLineSegment(sketch, "E452", {"start": v(-19, -12.5) * mm, "end": v(-19, -57.5) * mm, "construction": true});
            skLineSegment(sketch, "E453", {"start": v(-19, -35) * mm, "end": v(-11.75, -35) * mm, "construction": true});
            skSolve(sketch);
        }
        {
            var Q0;
            Q0=makeQuery(id+"F13.imprint","IMPRINT",FACE,{"disambiguationData":[TD([[makeQuery(id+"F13.imprint","IMPRINT",EDGE,{"derivedFrom":sQuery(id+"F13.wireOp",EDGE,"E449.bottom")}),-1.0]])]});
            extrude(context, id + "F14", {"entities" : qUnion([Q0]), "operationType" : NewBodyOperationType.REMOVE, "oppositeDirection" : true, "depth" : 4 * mm, "offsetDistance" : 25 * mm});
        }
    });
